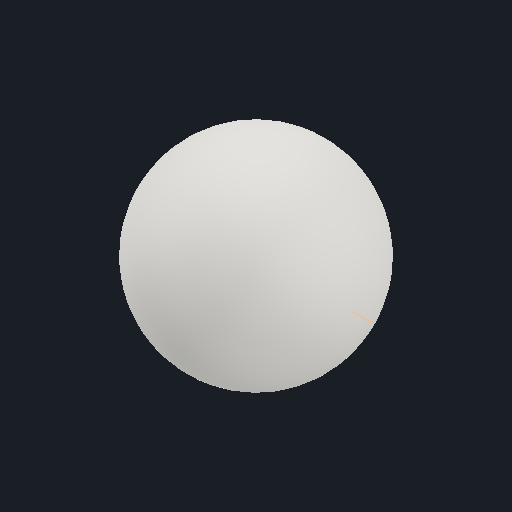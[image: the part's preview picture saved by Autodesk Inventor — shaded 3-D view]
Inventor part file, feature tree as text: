
AUTODESK INVENTOR PART (.ipt)
format: ipt  version: 2022 (Build 260153000, 153)  size: 123,904 bytes
history: native  units: mm
features: other x1, revolve x1, sketch x1
ambient origin geometry x8: Origin, YZ Plane, XZ Plane, XY Plane, X Axis, Y Axis, Z Axis, Center Point
bodies: Body1 (feature_tree)
feature tree (3):
  other  "Sólido1"
  revolve  "Revolución1"  Angle=90.0deg
  sketch  "Boceto1"  dims[d1=15.0mm d2=90.0deg]
